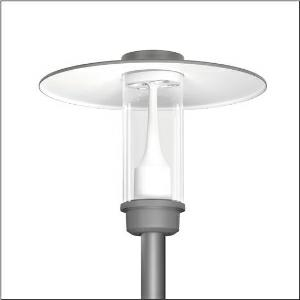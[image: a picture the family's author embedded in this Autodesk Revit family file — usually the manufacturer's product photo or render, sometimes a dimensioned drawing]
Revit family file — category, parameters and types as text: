
# Revit family: litepole_2_iq___st1_2a_5xa5425kf14hp_e686
name_source: partatom
category: Lighting Fixtures
units: mm (PartAtom-declared; Revit-internal decimal feet)

## family parameters
Cut with Voids When Loaded = No
Host = Face
Light Source = No
Part Type = Normal
Room Calculation Point = No
Round Connector Dimension = Use Diameter
Shared = No

## types (1)
- --- (1 x LED, 4980 lm, 33.6 W, 4000K)
    Apparent Load = 34 VA
    CIE Flux Codes = 22 59 92 98 100
    Color Rendering = 70
    Color Temperature = 4000K
    Default Elevation = 1800 mm
    Description = Litepole 2 iQ, mast luminaire, Module 540 iQ-SR, primary light control with 3 zone facetted reflector, of plastic, silver coated, highly specular, structured, primary optical cover: cover, of PMMA, transparent, light distribution: ST1.2a, light emission: direct distribution, primary light characteristic: asymmetric, installation type: post-top, LED, High Power LED, rated luminous flux: 4.980lm, luminous efficacy: 148lm/W, light colour: 740, colour temperature: 4000K, control gear: iQ Street-Remote, control: pre-setting: logarithmic dimming characteristic, Street-Remote, Auto-Match, Temp-Guard, Lumen-Switch, Night-Set, Smart-Wire, Light-Fading, Desk-Remote (wireless, voltage-free reading and setting of iQ features in the workshop via application-optimized NFC function/RFID function), optimised constant luminous flux control (CLO 2.0), with terminal, 6-pole, max. 2.5mm², mains connection: 230..240V, AC, 50/60Hz, start of lifetime: 34W, end of service life: 36W, reduction: 15W, luminaire housing, upper part, of aluminium, coated, Siteco® metallic grey (DB 702S), diameter: 750mm, height: 590mm, spigot size: d x l = 76 x 70mm (post-top) | with reducer (optional accessory) 60 x 70mm, mounting height: 3..5m, post-top mast mounting element, of diecast aluminium, coated, Siteco® metallic grey (DB 702S), Module 540 iQ-SR, traffic white (RAL 9016), equipment: Power, protection rating (complete): IP65, insulation class (complete): insulation class II (safety insulation), certification: CE, ENEC, VDE, packaging unit: 1 piece

Light Distribution: ST1.2a
    Height = 590 mm
    Lamp = 1 x LED
    Lamp Light Flux = 4980 lm
    Lamp Power = 33.6 W
    Lamp count = 1
    Length = 750 mm
    Luminous efficacy = 148 lm/W
    Manufacturer = Siteco
    ModVariant = No
    Model = 5XA5425KF14HP
    Number of Poles = 1
    OnlyDefault = Yes
    Power Factor = 1
    Product Name = Litepole 2 iQ | ST1.2a
    Product group = mast luminaire | pylon top
    ProductGroupID = 6100
    Protection Class = Protection class II
    Protection Degree = IP 65
    RLX_Detail_Level = 1
    RLX_Emergency_Light_Flux = 0 lm
    RLX_Emergency_Type = 0
    RLX_Emergency_Type_DB = No
    RlxData = <blob elided: 31885 chars, md5=1e8009de>
    Socket = socket
    Standby Power = 0 W
    System Light Flux = 4980 lm
    System Power = 34 W
    Type Comments = factory setting: luminous flux: 100 % | dim-lin: 254 | 695 mA
    Type Image = l_1006518.jpg
    URL = http://relux.com
    VarID = @adj_213521
    Voltage = 0 V
    Weight = 0.00 kg
    Width = 0 mm  [stored 0 ft]

note: [stored X ft] marks values corroborated as IEEE doubles in the binary element streams (Revit-internal decimal feet)

## geometry (parser evidence)
native form markers: Blend x4, Sweep x13
no freeform markers — native parametric forms only
